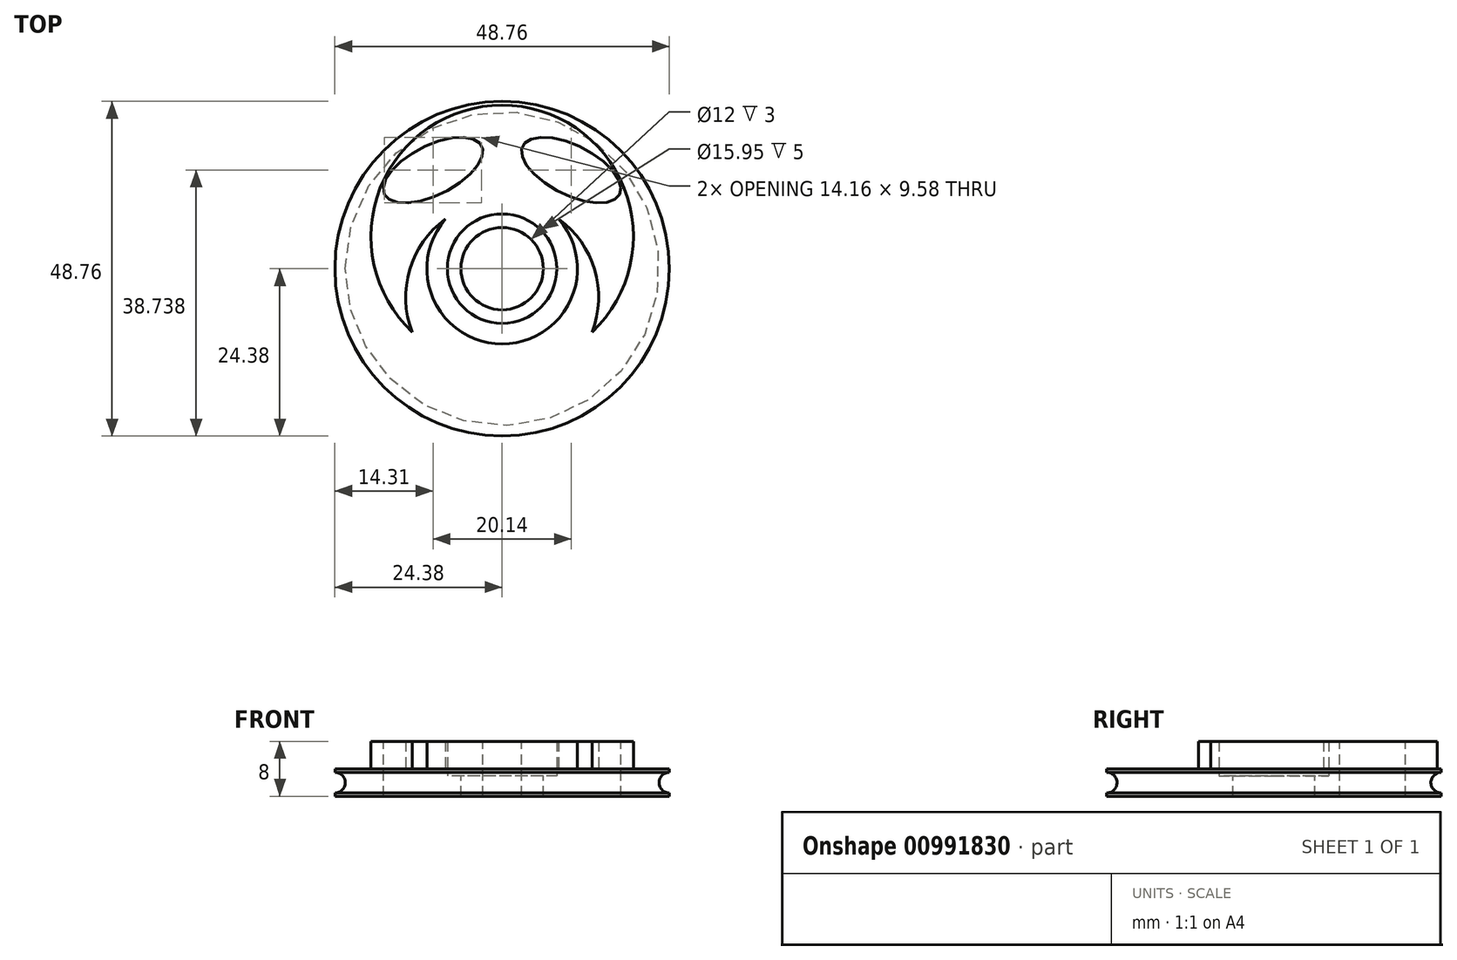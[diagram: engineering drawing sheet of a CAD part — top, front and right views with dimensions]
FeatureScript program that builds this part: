
annotation { "Feature Type Name" : "Feature", "Feature Type Description" : "" }
export const myFeature = defineFeature(function(context is Context, id is Id, definition is map)
    precondition{}
    {
        {
            var Q0;
            Q0=qCreatedBy(makeId("Top.planeOp"),FACE);
            var sketch = newSketch(context, id + "F0", { "sketchPlane" : qUnion([Q0])});
            skCircle(sketch, "E0", {"center": v(0, 0) * mm, "radius": 24.38 * mm});
            skSolve(sketch);
        }
        {
            var Q0;
            Q0=makeQuery(id+"F0.imprint","IMPRINT",FACE,{"disambiguationData":[TD([[makeQuery(id+"F0.imprint","IMPRINT",EDGE,{"derivedFrom":sQuery(id+"F0.wireOp",EDGE,"E0")}),1.0]])]});
            extrude(context, id + "F1", {"entities" : qUnion([Q0]), "depth" : 4 * mm, "offsetDistance" : 25.4 * mm});
        }
        {
            var Q0;
            Q0=makeQuery(id+"F1.opExtrude","CAP_FACE",FACE,{"disambiguationData":[OSD([sQuery(id+"F0.wireOp",EDGE,"E0"),sQuery(id+"F0.wireOp",EDGE,"n39IqKt5-bk1q-LU1x-fgod-8OyBNiFTd7FZ")])],"isStart":false});
            var sketch = newSketch(context, id + "F2", { "sketchPlane" : qUnion([Q0])});
            skCircle(sketch, "E1", {"center": v(0, 0) * mm, "radius": 7.97 * mm});
            skCircle(sketch, "E2.0", {"center": v(0, 0) * mm, "radius": 10.97 * mm});
            skSolve(sketch);
        }
        {
            var Q0;
            Q0=qSketchRegion(id+"F2",true);
            extrude(context, id + "F3", {"entities" : qUnion([Q0]), "operationType" : NewBodyOperationType.ADD, "depth" : 4 * mm, "offsetDistance" : 25.4 * mm});
        }
        {
            var Q0;
            Q0=makeQuery(id+"F3.boolean.opBoolean","SPLIT",FACE,{"disambiguationData":[TD([makeQuery(id+"F3.opExtrude","SWEPT_FACE",FACE,{"disambiguationData":[OSD([sQuery(id+"F2.wireOp",EDGE,"E1")])]})])],"derivedFrom":makeQuery(id+"F1.opExtrude","CAP_FACE",FACE,{"disambiguationData":[OSD([sQuery(id+"F0.wireOp",EDGE,"E0")])],"isStart":false})});
            var sketch = newSketch(context, id + "F4", { "sketchPlane" : qUnion([Q0])});
            skCircle(sketch, "E3", {"center": v(0, 0) * mm, "radius": 6 * mm});
            skSolve(sketch);
        }
        {
            var Q0;
            Q0=makeQuery(id+"F4.imprint","IMPRINT",FACE,{"disambiguationData":[TD([[makeQuery(id+"F4.imprint","IMPRINT",EDGE,{"derivedFrom":sQuery(id+"F4.wireOp",EDGE,"E3")}),1.0]])]});
            var Q1;
            Q1=makeQuery(id+"F4.imprint","IMPRINT",FACE,{"disambiguationData":[TD([[makeQuery(id+"F4.imprint","IMPRINT",EDGE,{"derivedFrom":makeQuery(id+"FgYK8jIepfClWtA_1.opExtrude","CAP_EDGE",EDGE,{"disambiguationData":[OSD([sQuery(id+"F8DXjnVyigKkjng_1.wireOp",EDGE,"EUjAMsCd-Zx2B-3j4q-cP5o-T3GrjTijNDqK")])],"isStart":false})}),1.0]])]});
            extrude(context, id + "F5", {"entities" : qUnion([Q0, Q1]), "operationType" : NewBodyOperationType.REMOVE, "oppositeDirection" : true, "depth" : 9 * mm, "offsetDistance" : 25.4 * mm});
        }
        {
            var Q0;
            Q0=qCreatedBy(makeId("Front.planeOp"),FACE);
            var sketch = newSketch(context, id + "F6", { "sketchPlane" : qUnion([Q0])});
            skCircle(sketch, "E4", {"center": v(-24.38, 2) * mm, "radius": 1.5 * mm});
            skLineSegment(sketch, "E5.bottom", {"start": v(-22.88, 0.65) * mm, "end": v(-25.02, 0.65) * mm});
            skLineSegment(sketch, "E5.top", {"start": v(-22.88, 3.35) * mm, "end": v(-25.02, 3.35) * mm});
            skLineSegment(sketch, "E5.left", {"start": v(-22.88, 0.65) * mm, "end": v(-22.88, 3.35) * mm});
            skLineSegment(sketch, "E5.right", {"start": v(-25.73, 1.35) * mm, "end": v(-25.73, 2.65) * mm});
            skLineSegment(sketch, "E6", {"start": v(0, 19.1) * mm, "end": v(0, -12.61) * mm, "construction": true});
            skLineSegment(sketch, "E7", {"start": v(-24.37, 3.35) * mm, "end": v(-22.88, 2) * mm});
            skLineSegment(sketch, "E8", {"start": v(-22.88, 2) * mm, "end": v(-24.38, 0.65) * mm});
            skLineSegment(sketch, "E9", {"start": v(-24.38, 0.65) * mm, "end": v(-24.37, 3.35) * mm});
            skSolve(sketch);
        }
        {
            var Q0;
            {var subQ0=sQuery(id+"F6.wireOp",EDGE,"E5.top");var subQ1=sQuery(id+"F6.wireOp",EDGE,"E4");var subQ2=makeQuery(id+"F6.imprint","INTERSECT",VERTEX,{"disambiguationData":[OD(0.0)],"derivedFrom":[subQ1,subQ0]});Q0=makeQuery(id+"F6.imprint","IMPRINT",FACE,{"disambiguationData":[TD([[makeQuery(id+"F6.imprint","IMPRINT",EDGE,{"disambiguationData":[TD([[subQ2,1.0]])],"derivedFrom":subQ1}),1.0]])]});}
            var Q1;
            {var subQ0=sQuery(id+"F6.wireOp",EDGE,"E5.bottom");var subQ1=sQuery(id+"F6.wireOp",EDGE,"E4");var subQ2=makeQuery(id+"F6.imprint","INTERSECT",VERTEX,{"disambiguationData":[OD(0.0)],"derivedFrom":[subQ1,subQ0]});Q1=makeQuery(id+"F6.imprint","IMPRINT",FACE,{"disambiguationData":[TD([[makeQuery(id+"F6.imprint","IMPRINT",EDGE,{"disambiguationData":[TD([[subQ2,-1.0]])],"derivedFrom":subQ1}),1.0]])]});}
            var Q2;
            {var subQ4=sQuery(id+"F6.wireOp",EDGE,"E5.right");Q2=makeQuery(id+"F6.imprint","IMPRINT",FACE,{"disambiguationData":[TD([[makeQuery(id+"F6.imprint","IMPRINT",EDGE,{"derivedFrom":subQ4}),-1.0]])]});}
            var Q3;
            {var subQ0=sQuery(id+"F6.wireOp",EDGE,"E7");Q3=makeQuery(id+"F6.imprint","IMPRINT",FACE,{"disambiguationData":[TD([[makeQuery(id+"F6.imprint","IMPRINT",EDGE,{"derivedFrom":subQ0}),1.0]])]});}
            var Q4;
            Q4=makeQuery(id+"F6.imprint","IMPRINT",FACE,{"disambiguationData":[TD([[makeQuery(id+"F6.imprint","IMPRINT",EDGE,{"derivedFrom":sQuery(id+"F6.wireOp",EDGE,"E7")}),-1.0]])]});
            var Q5;
            {var subQ0=sQuery(id+"F6.wireOp",EDGE,"E8");Q5=makeQuery(id+"F6.imprint","IMPRINT",FACE,{"disambiguationData":[TD([[makeQuery(id+"F6.imprint","IMPRINT",EDGE,{"derivedFrom":subQ0}),1.0]])]});}
            var Q6;
            Q6=sQuery(id+"F6.wireOp",EDGE,"E6");
            revolve(context, id + "F7", {"operationType" : NewBodyOperationType.REMOVE, "surfaceOperationType" : NewSurfaceOperationType.NEW, "entities" : qUnion([Q0, Q1, Q2, Q3, Q4, Q5]), "axis" : qUnion([Q6]), "revolveType" : RevolveType.FULL, "oppositeDirection" : true});
        }
        {
            var Q0;
            Q0=makeQuery(id+"F3.boolean.opBoolean","SPLIT",FACE,{"disambiguationData":[TD([makeQuery(id+"F3.opExtrude","SWEPT_FACE",FACE,{"disambiguationData":[OSD([sQuery(id+"F2.wireOp",EDGE,"E1")])]})])],"derivedFrom":makeQuery(id+"F1.opExtrude","CAP_FACE",FACE,{"disambiguationData":[OSD([sQuery(id+"F0.wireOp",EDGE,"E0")])],"isStart":false})});
            extrude(context, id + "F8", {"entities" : qUnion([Q0]), "operationType" : NewBodyOperationType.REMOVE, "oppositeDirection" : true, "depth" : 1 * mm, "offsetDistance" : 25 * mm});
        }
        {
            var Q0;
            {var subQ0=sQuery(id+"F0.wireOp",EDGE,"E0");Q0=makeQuery(id+"F3.boolean.opBoolean","SPLIT",FACE,{"disambiguationData":[TD([makeQuery(id+"F1.opExtrude","SWEPT_FACE",FACE,{"disambiguationData":[OSD([subQ0])]})])],"derivedFrom":makeQuery(id+"F1.opExtrude","CAP_FACE",FACE,{"disambiguationData":[OSD([subQ0])],"isStart":false})});}
            var sketch = newSketch(context, id + "F9", { "sketchPlane" : qUnion([Q0])});
            skEllipse(sketch, "E10", {"center": v(-10.07, 14.36) * mm, "majorRadius": 7.91 * mm, "minorRadius": 3.61 * mm, "majorAxis": v(-0.9, -0.45)});
            skEllipse(sketch, "E11.MirrorC", {"center": v(10.07, 14.36) * mm, "majorRadius": 7.91 * mm, "minorRadius": 3.61 * mm, "majorAxis": v(0.9, -0.45)});
            skCircle(sketch, "E12", {"center": v(0, 4.7) * mm, "radius": 19.13 * mm});
            skCircle(sketch, "E13", {"center": v(0, -4.15) * mm, "radius": 14.06 * mm});
            skSolve(sketch);
        }
        {
            var Q0;
            Q0=makeQuery(id+"F9.imprint","IMPRINT",FACE,{"disambiguationData":[TD([[makeQuery(id+"F9.imprint","IMPRINT",EDGE,{"derivedFrom":sQuery(id+"F9.wireOp",EDGE,"E10")}),1.0]])]});
            var Q1;
            Q1=makeQuery(id+"F9.imprint","IMPRINT",FACE,{"disambiguationData":[TD([[makeQuery(id+"F9.imprint","IMPRINT",EDGE,{"derivedFrom":sQuery(id+"F9.wireOp",EDGE,"E11.MirrorC")}),1.0]])]});
            extrude(context, id + "F10", {"entities" : qUnion([Q0, Q1]), "operationType" : NewBodyOperationType.REMOVE, "oppositeDirection" : true, "depth" : 25 * mm, "offsetDistance" : 25 * mm});
        }
        {
            var Q0;
            Q0=makeQuery(id+"F9.imprint","IMPRINT",FACE,{"disambiguationData":[TD([[makeQuery(id+"F9.imprint","IMPRINT",EDGE,{"derivedFrom":sQuery(id+"F9.wireOp",EDGE,"E10")}),-1.0]])]});
            extrude(context, id + "F11", {"entities" : qUnion([Q0]), "operationType" : NewBodyOperationType.ADD, "depth" : 2 * mm, "offsetDistance" : 25 * mm});
        }
        {
            var Q0;
            {var subQ0=sQuery(id+"F9.wireOp",EDGE,"E13");var subQ1=sQuery(id+"F9.wireOp",EDGE,"E12");var subQ2=makeQuery(id+"F9.imprint","INTERSECT",VERTEX,{"disambiguationData":[OD(0.0)],"derivedFrom":[subQ1,subQ0]});Q0=makeQuery(id+"F9.imprint","IMPRINT",FACE,{"disambiguationData":[TD([[makeQuery(id+"F9.imprint","IMPRINT",EDGE,{"disambiguationData":[TD([[subQ2,-1.0]])],"derivedFrom":subQ1}),1.0]])]});}
            extrude(context, id + "F12", {"entities" : qUnion([Q0]), "operationType" : NewBodyOperationType.ADD, "depth" : 4 * mm, "offsetDistance" : 25 * mm});
        }
    });
